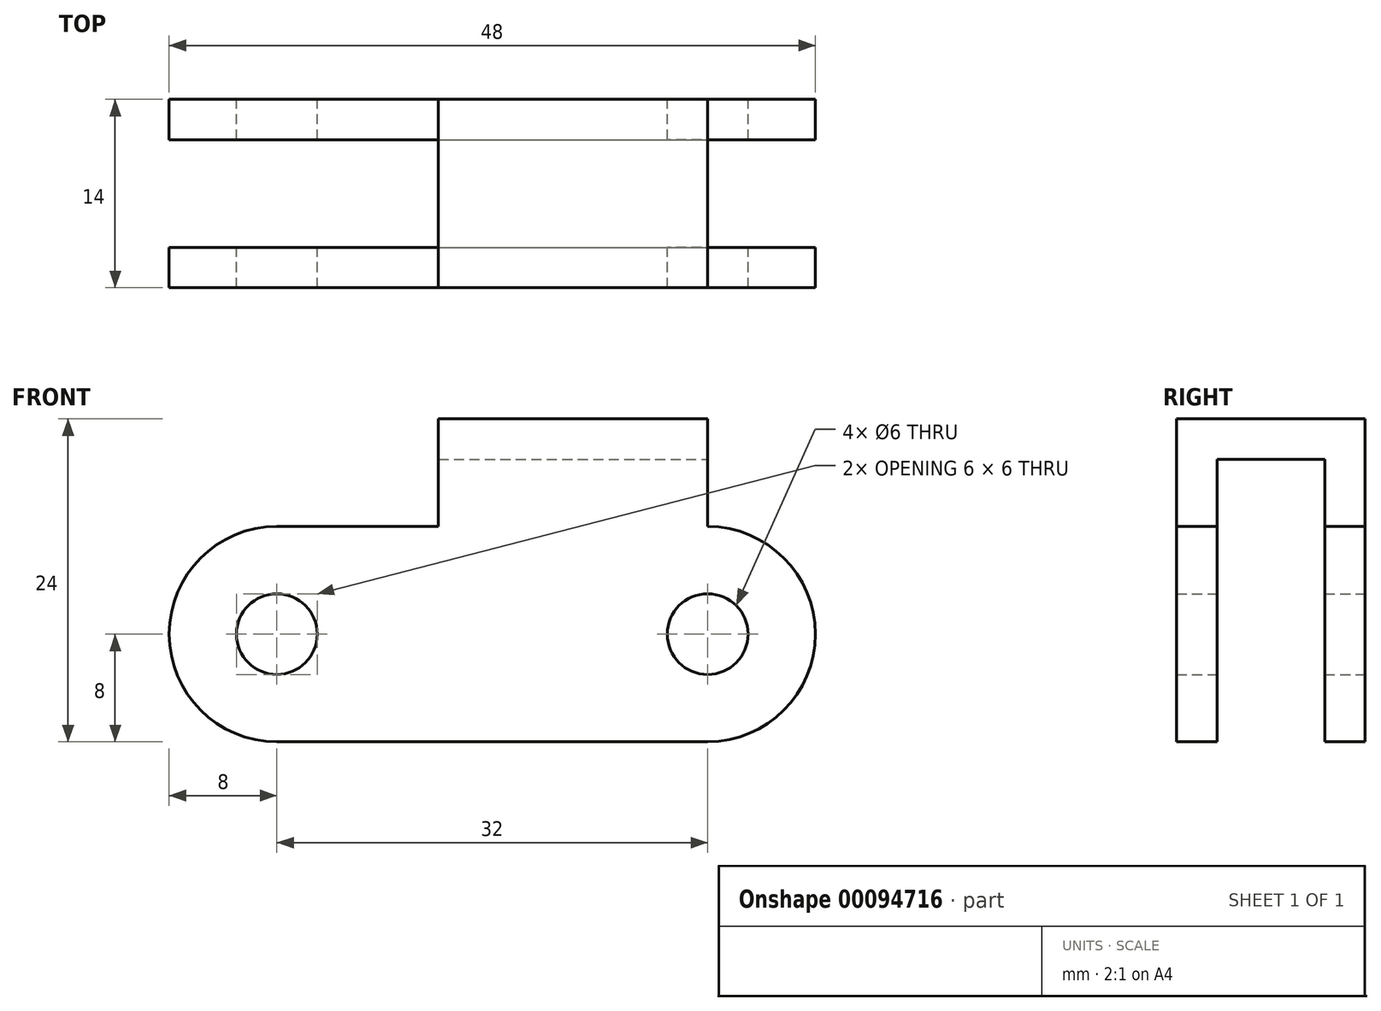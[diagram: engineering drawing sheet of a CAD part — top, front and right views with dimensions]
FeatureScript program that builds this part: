
annotation { "Feature Type Name" : "Feature", "Feature Type Description" : "" }
export const myFeature = defineFeature(function(context is Context, id is Id, definition is map)
    precondition{}
    {
        {
            var Q0;
            Q0=qCreatedBy(makeId("Front.planeOp"),FACE);
            var sketch = newSketch(context, id + "F0", { "sketchPlane" : qUnion([Q0])});
            skLineSegment(sketch, "E0", {"start": v(0, 0) * mm, "end": v(-32, 0) * mm, "construction": true});
            skArc(sketch, "E1.0.startCap", {"start": v(0, 8) * mm, "mid": v(8, 0) * mm, "end": v(0, -8) * mm});
            skArc(sketch, "E1.0.endCap", {"start": v(-32, -8) * mm, "mid": v(-40, 0) * mm, "end": v(-32, 8) * mm});
            skLineSegment(sketch, "E1.0.left", {"start": v(0, -8) * mm, "end": v(-32, -8) * mm});
            skLineSegment(sketch, "E1.0.right", {"start": v(0, 8) * mm, "end": v(-32, 8) * mm});
            skCircle(sketch, "E2", {"center": v(-32, 0) * mm, "radius": 3 * mm});
            skCircle(sketch, "E3", {"center": v(0, 0) * mm, "radius": 3 * mm});
            skLineSegment(sketch, "E4.top", {"start": v(-20, 16) * mm, "end": v(0, 16) * mm});
            skLineSegment(sketch, "E4.left", {"start": v(-20, 8) * mm, "end": v(-20, 16) * mm});
            skLineSegment(sketch, "E4.right", {"start": v(0, 8) * mm, "end": v(0, 16) * mm});
            skSolve(sketch);
        }
        {
            var Q0;
            Q0 = qSketchRegion(id + "F0", true);
            extrude(context, id + "F1", {"entities" : qUnion([Q0]), "endBound" : BoundingType.SYMMETRIC, "depth" : 14 * mm});
        }
        {
            var Q0;
            Q0=qCreatedBy(makeId("Right.planeOp"),FACE);
            var sketch = newSketch(context, id + "F2", { "sketchPlane" : qUnion([Q0])});
            skLineSegment(sketch, "E5.bottom", {"start": v(4, -13) * mm, "end": v(-4, -13) * mm});
            skLineSegment(sketch, "E5.top", {"start": v(4, 13) * mm, "end": v(-4, 13) * mm});
            skLineSegment(sketch, "E5.left", {"start": v(4, -13) * mm, "end": v(4, 13) * mm});
            skLineSegment(sketch, "E5.right", {"start": v(-4, -13) * mm, "end": v(-4, 13) * mm});
            skPoint(sketch, "E5.middle", {"position": v(0, 0) * mm});
            skSolve(sketch);
        }
        {
            var Q0;
            Q0=makeQuery(id+"F2.imprint","IMPRINT",FACE,{"disambiguationData":[TD([[makeQuery(id+"F2.imprint","IMPRINT",EDGE,{"derivedFrom":sQuery(id+"F2.wireOp",EDGE,"E5.bottom")}),-1.0]])]});
            extrude(context, id + "F3", {"entities" : qUnion([Q0]), "operationType" : NewBodyOperationType.REMOVE, "endBound" : BoundingType.SYMMETRIC, "oppositeDirection" : true, "depth" : 117.8 * mm});
        }
    });
